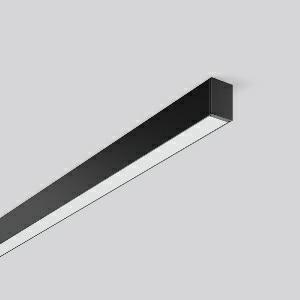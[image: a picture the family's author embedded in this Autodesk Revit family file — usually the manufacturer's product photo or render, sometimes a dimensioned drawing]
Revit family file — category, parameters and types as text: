
# Revit family: less_is_more_27_312198_003_76_7ffd
name_source: partatom
category: Lighting Fixtures
units: mm (PartAtom-declared; Revit-internal decimal feet)

## family parameters
Cut with Voids When Loaded = No
Host = Face
Light Source = No
Part Type = Normal
Room Calculation Point = No
Round Connector Dimension = Use Diameter
Shared = No

## types (1)
- LESS IS MORE 27 (1 x LED Modul 830, 1900 lm, 3000)
    Apparent Load = 35 VA
    CIE Flux Codes = 48 79 96 100 100
    Color Rendering = 80
    Color Temperature = 3000
    Default Elevation = 1800 mm
    Description = Series: LESS IS MORE 27
Ceiling and wall luminaire with slim design. Housing: extruded aluminium profile, powder-coated. End cap aluminium powder-coated. Diffuser made of non-yellowing plastic (PMMA), opal. Suitable for Ceiling mounting, Wall (surface). External driver with connecting cable. 
Colour: deep black, matt (RAL 9005)
Length: 1212 mm
Width: 28 mm
Height: 38 mm
Lamp: LED
Socket: without socket
Colour temperature: 3000K
Colour rendering index (CRI): 82
System power: 35 W
Rated luminous flux: 1900 lm
Luminous efficiency: 54 lm/W
Control gear: Voltage converter, DALI dim.
Protection class: II
Type of protection: IP 20
    Height = 38 mm
    Lamp = 1 x LED Modul 830
    Lamp Light Flux = 1900 lm
    Lamp count = 1
    Length = 1212 mm
    Lifetime = 50000 h
    Luminous efficacy = 54 lm/W
    Manufacturer = RZB
    ModVariant = No
    Model = 312198.003.76
    Mounting Place = Ceiling, Wall
    Mounting Type = Surface mounted
    Number of Poles = 1
    OnlyDefault = Yes
    Power Factor = 1
    Product Name = LESS IS MORE 27
    Product group = Surface mounted LED linear luminaires
    ProductGroupID = 307
    Protection Class = Protection class II
    Protection Degree = IP 20
    RLX_Detail_Level = 1
    RLX_Emergency_Light_Flux = 0 lm
    RLX_Emergency_Type = 0
    RLX_Emergency_Type_DB = No
    RlxData = <blob elided: 28721 chars, md5=7fb17494>
    Socket = socket
    Standby Power = 0 W
    System Light Flux = 1900 lm
    System Power = 35 W
    Type Comments = Product without accessories
    Type Image = 312196.003.jpg
    URL = http://relux.com
    VarID = ---
    Voltage = 230 V
    Voltage Range = 220-240 V
    Weight = 0.00 kg
    Width = 28 mm

## geometry (parser evidence)
native form markers: Blend x4, Sweep x12
no freeform markers — native parametric forms only
